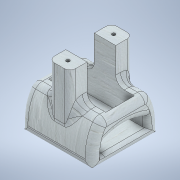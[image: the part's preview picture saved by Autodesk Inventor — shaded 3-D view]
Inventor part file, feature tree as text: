
AUTODESK INVENTOR PART (.ipt)
format: ipt  version: 2021 (Build 250183000, 183)  size: 958,464 bytes
history: native  units: mm
features: extrude x24, sketch x24, fillet x7, projected_geometry x6, plane x1, mirror x1
ambient origin geometry x8: Origin, YZ Plane, XZ Plane, XY Plane, X Axis, Y Axis, Z Axis, Center Point
bodies: Solid1 (feature_tree)
feature tree (63):
  extrude  "Extrusion1"  Depth=39.0mm
  extrude  "Extrusion2"  Depth=8.0mm
  plane  "Work Plane2"
  mirror  "Mirror1"
  extrude  "Extrusion3"  Depth=8.0mm
  extrude  "Extrusion4"  Depth=4.0mm TaperAngle=0.0deg
  extrude  "Extrusion5"  Depth=10.0mm
  extrude  "Extrusion6"  Depth=4.0mm TaperAngle=0.0deg
  extrude  "Extrusion7"  Depth=19.0mm
  extrude  "Extrusion8"  Depth=4.0mm TaperAngle=0.0deg
  extrude  "Extrusion9"  Depth=4.0mm TaperAngle=0.0deg
  extrude  "Extrusion10"  Depth=2.0mm TaperAngle=0.0deg
  extrude  "Extrusion11"  Depth=12.5mm
  extrude  "Extrusion12"  Depth=4.0mm
  extrude  "Extrusion13"  Depth=7.9mm
  extrude  "Extrusion14"  Depth=7.9mm
  extrude  "Extrusion15"  Depth=6.0mm TaperAngle=0.0deg
  extrude  "Extrusion16"  Depth=8.5mm TaperAngle=0.0deg
  extrude  "Extrusion17"  Depth=8.5mm TaperAngle=0.0deg
  fillet  "Fillet6"  Radius=36.0mm
  fillet  "Fillet7"  Radius=8.5mm
  fillet  "Fillet8"  Radius=15.0mm
  extrude  "Extrusion18"  Depth=6.0mm
  fillet  "Fillet9"  Radius=6.0mm
  extrude  "Extrusion20"  Depth=8.5mm TaperAngle=0.0deg
  extrude  "Extrusion21"  Depth=7.9mm
  extrude  "Extrusion22"  Depth=7.9mm
  extrude  "Extrusion23"  Depth=11.0mm
  fillet  "Fillet14"  Radius=11.0mm
  fillet  "Fillet15"  Radius=11.0mm
  fillet  "Fillet16"  Radius=11.0mm
  extrude  "Extrusion24"  Depth=11.0mm
  extrude  "Extrusion25"  Depth=10.0mm
  sketch  "Sketch1"  dims[d0=15.0mm d1=39.0mm]
  sketch  "Sketch2"  dims[d2=4.0mm d3=0.0mm d5=8.0mm]
  sketch  "Sketch3"  dims[d6=15.0mm d7=8.0mm]
  sketch  "Sketch4"  dims[d8=14.0mm d9=4.0mm d10=0.0mm]
  sketch  "Sketch5"  dims[d12=10.0mm d13=27.0mm]
  sketch  "Sketch7"  dims[d14=28.0mm d15=4.0mm d16=0.0mm]
  sketch  "Sketch8"  dims[d17=28.0mm d18=19.0mm]
  sketch  "Sketch10"  dims[d19=4.0mm d20=0.0mm d21=4.0mm d22=0.0mm]
  projected_geometry  "Projected Loop2"
  sketch  "Sketch11"  dims[d23=13.0mm d24=0.0mm d25=4.0mm d26=0.0mm]
  projected_geometry  "Projected Loop3"
  sketch  "Sketch12"  dims[d27=3.0mm d28=0.0mm d29=2.0mm d30=0.0mm]
  projected_geometry  "Projected Loop4"
  sketch  "Sketch14"  dims[d31=2.0mm d32=0.0mm d35=12.5mm]
  sketch  "Sketch15"  dims[d36=11.5mm d37=4.0mm]
  sketch  "Sketch18"  dims[d38=6.0mm d39=7.9mm]
  sketch  "Sketch19"  dims[d40=7.9mm d41=7.9mm]
  projected_geometry  "Projected Loop9"
  sketch  "Sketch20"  dims[d42=7.9mm d43=6.0mm d44=0.0mm]
  projected_geometry  "Projected Loop10"
  sketch  "Sketch21"  dims[d45=0.2mm d46=0.0mm d49=8.5mm d50=56.5mm d51=0.0mm d52=0.0mm]
  sketch  "Sketch22"  dims[d53=8.5mm d54=0.0mm d55=8.5mm d56=0.0mm d57=36.0mm d58=8.5mm d59=0.0mm d61=15.0mm d62=0.0mm]
  sketch  "Sketch23"  dims[d63=4.0mm d64=6.0mm d65=6.0mm]
  projected_geometry  "Projected Loop12"
  sketch  "Sketch25"  dims[d66=30.0mm d70=8.5mm d71=0.0mm]
  sketch  "Sketch26"  dims[d72=3.0mm d79=7.9mm]
  sketch  "Sketch27"  dims[d80=7.9mm d81=7.9mm]
  sketch  "Sketch28"  dims[d82=7.9mm d83=11.0mm d84=11.0mm d85=11.0mm d86=11.0mm]
  sketch  "Sketch29"  dims[d88=11.0mm d89=11.0mm]
  sketch  "Sketch30"  dims[d90=11.0mm d91=11.0mm d92=2.4mm d93=2.4mm d94=15.0mm d95=0.0mm d96=21.0mm d97=2.2mm d98=0.0mm d99=6.0mm d101=2.2mm d102=0.0mm d103=15.0mm d104=0.0mm d105=5.0mm d106=5.0mm d107=5.0mm d108=6.5mm d109=15.0mm d110=0.0mm d111=10.0mm d112=0.0mm]
